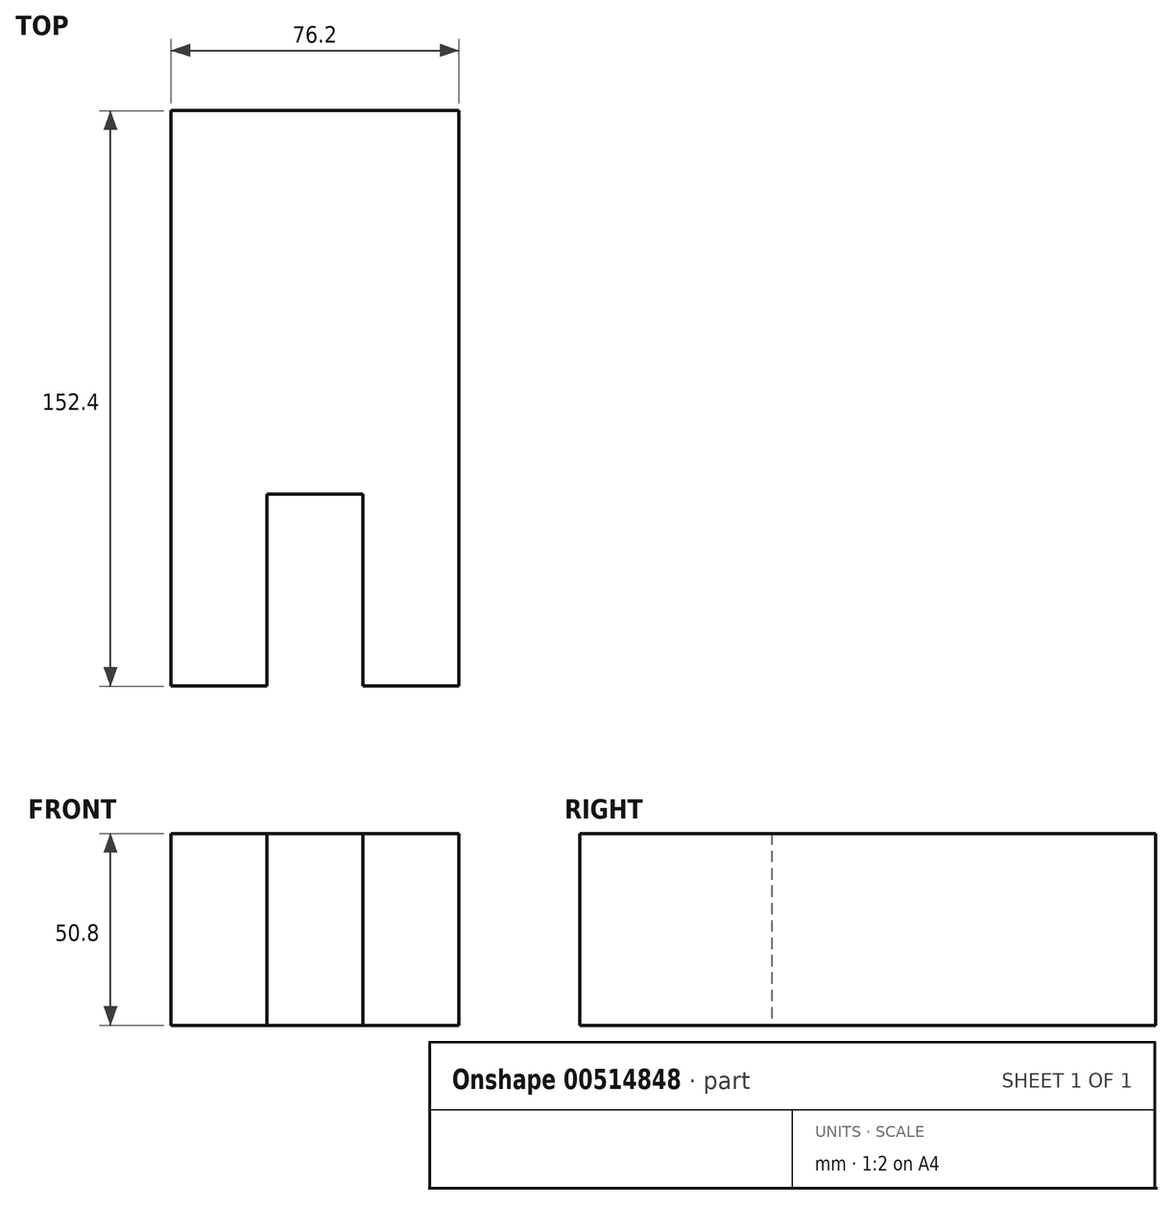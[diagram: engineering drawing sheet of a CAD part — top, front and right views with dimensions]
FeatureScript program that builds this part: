
annotation { "Feature Type Name" : "Feature", "Feature Type Description" : "" }
export const myFeature = defineFeature(function(context is Context, id is Id, definition is map)
    precondition{}
    {
        {
            var Q0;
            Q0=qCreatedBy(makeId("Top.planeOp"),FACE);
            var sketch = newSketch(context, id + "F0", { "sketchPlane" : qUnion([Q0])});
            skLineSegment(sketch, "E0", {"start": v(-32.56, 133.1) * mm, "end": v(43.64, 133.1) * mm});
            skLineSegment(sketch, "E1", {"start": v(-32.56, 133.1) * mm, "end": v(-32.56, -19.3) * mm});
            skLineSegment(sketch, "E2", {"start": v(43.64, 133.1) * mm, "end": v(43.64, -19.3) * mm});
            skLineSegment(sketch, "E3", {"start": v(43.64, -19.3) * mm, "end": v(18.24, -19.3) * mm});
            skLineSegment(sketch, "E4", {"start": v(18.24, -19.3) * mm, "end": v(18.24, 31.5) * mm});
            skLineSegment(sketch, "E5", {"start": v(18.24, 31.5) * mm, "end": v(-7.16, 31.5) * mm});
            skLineSegment(sketch, "E6", {"start": v(-7.16, 31.5) * mm, "end": v(-7.16, -19.3) * mm});
            skLineSegment(sketch, "E7", {"start": v(-32.56, -19.3) * mm, "end": v(-7.16, -19.3) * mm});
            skSolve(sketch);
        }
        {
            var Q0;
            Q0 = qSketchRegion(id + "F0", true);
            extrude(context, id + "F1", {"entities" : qUnion([Q0]), "depth" : 50.8 * mm, "offsetDistance" : 25.4 * mm});
        }
    });
